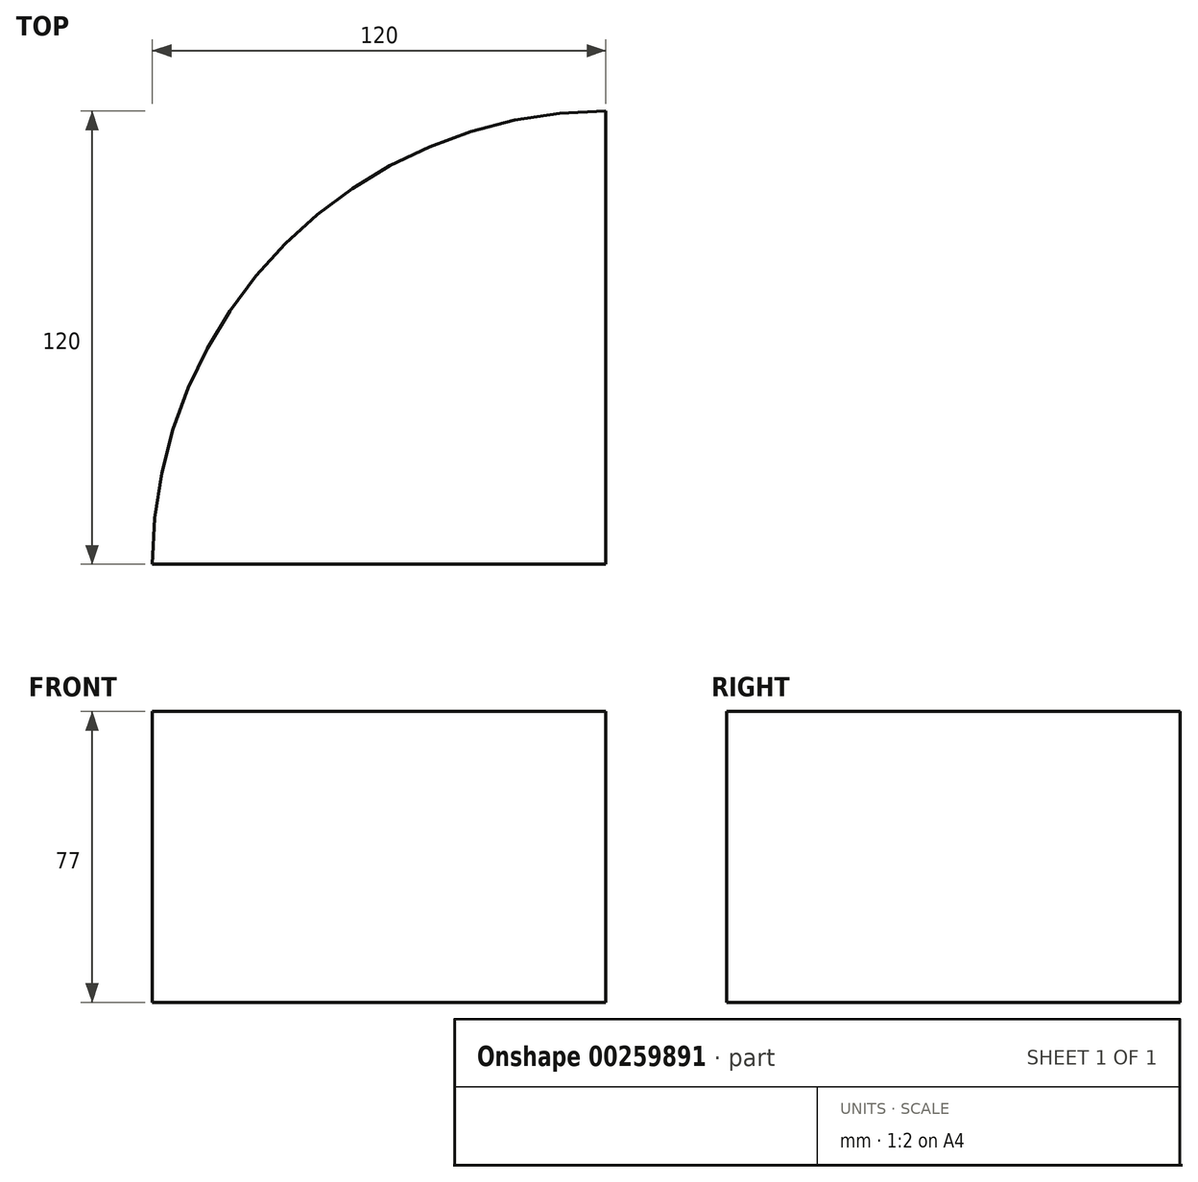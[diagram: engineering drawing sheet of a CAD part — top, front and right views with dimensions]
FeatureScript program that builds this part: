
annotation { "Feature Type Name" : "Feature", "Feature Type Description" : "" }
export const myFeature = defineFeature(function(context is Context, id is Id, definition is map)
    precondition{}
    {
        {
            var Q0;
            Q0=qCreatedBy(makeId("Top.planeOp"),FACE);
            var sketch = newSketch(context, id + "F0", { "sketchPlane" : qUnion([Q0])});
            skLineSegment(sketch, "E0", {"start": v(-41.02, 30.01) * mm, "end": v(78.98, 30.01) * mm});
            skLineSegment(sketch, "E1", {"start": v(78.98, 185.26) * mm, "end": v(78.98, 30.01) * mm});
            skArc(sketch, "E2", {"start": v(-41.02, 30.01) * mm, "mid": v(-5.87, 114.87) * mm, "end": v(78.98, 150.01) * mm});
            skLineSegment(sketch, "E3", {"start": v(78.98, 30.01) * mm, "end": v(-76.27, 30.01) * mm});
            skArc(sketch, "E4", {"start": v(-76.27, 30.01) * mm, "mid": v(-30.8, 139.8) * mm, "end": v(78.98, 185.26) * mm});
            skSolve(sketch);
        }
        {
            var Q0;
            {var subQ2=sQuery(id+"F0.wireOp",EDGE,"E2");Q0=makeQuery(id+"F0.imprint","IMPRINT",FACE,{"disambiguationData":[TD([[makeQuery(id+"F0.imprint","IMPRINT",EDGE,{"derivedFrom":subQ2}),1.0]])]});}
            extrude(context, id + "F1", {"entities" : qUnion([Q0]), "endBound" : BoundingType.SYMMETRIC, "depth" : 77 * mm});
        }
    });
